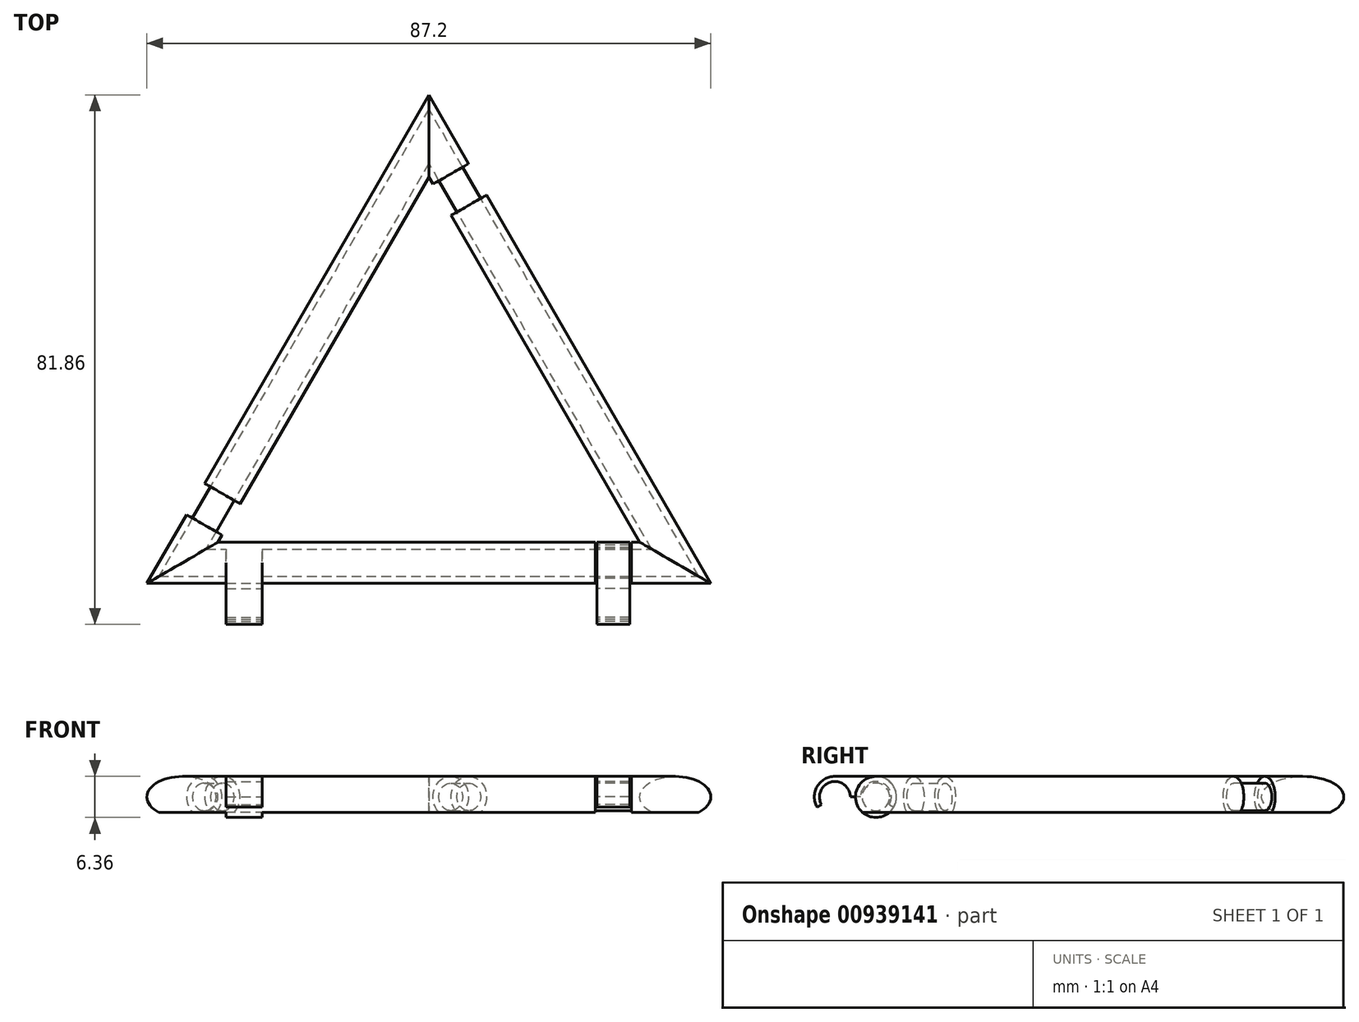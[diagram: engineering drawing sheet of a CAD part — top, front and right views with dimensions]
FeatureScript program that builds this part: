
annotation { "Feature Type Name" : "Feature", "Feature Type Description" : "" }
export const myFeature = defineFeature(function(context is Context, id is Id, definition is map)
    precondition{}
    {
        {
            var Q0;
            Q0=qCreatedBy(makeId("Top.planeOp"),FACE);
            var sketch = newSketch(context, id + "F0", { "sketchPlane" : qUnion([Q0])});
            skCircle(sketch, "E0.cCircle", {"center": v(0, 0) * mm, "radius": 44 * mm, "construction": true});
            skLineSegment(sketch, "E0.0", {"start": v(0, 44) * mm, "end": v(38.1, -22) * mm});
            skLineSegment(sketch, "E0.1", {"start": v(38.1, -22) * mm, "end": v(-38.1, -22) * mm});
            skLineSegment(sketch, "E0.2", {"start": v(-38.1, -22) * mm, "end": v(0, 44) * mm});
            skPoint(sketch, "E1", {"position": v(31.33, -22) * mm});
            skPoint(sketch, "E2", {"position": v(34.72, -16.13) * mm});
            skPoint(sketch, "E3", {"position": v(-31.33, -22) * mm});
            skPoint(sketch, "E4", {"position": v(-34.72, -16.13) * mm});
            skPoint(sketch, "E5", {"position": v(-3.38, 38.13) * mm});
            skPoint(sketch, "E6", {"position": v(3.38, 38.13) * mm});
            skPoint(sketch, "E7", {"position": v(6.05, 33.51) * mm});
            skPoint(sketch, "E8", {"position": v(-6.18, 33.3) * mm});
            skPoint(sketch, "E9", {"position": v(31.92, -11.3) * mm});
            skPoint(sketch, "E10", {"position": v(25.74, -22) * mm});
            skPoint(sketch, "E11", {"position": v(-25.74, -22) * mm});
            skPoint(sketch, "E12", {"position": v(-32.05, -11.52) * mm});
            skPoint(sketch, "E13", {"position": v(-31.08, -22) * mm});
            skPoint(sketch, "E14", {"position": v(-26, -22) * mm});
            skPoint(sketch, "E15", {"position": v(-34.59, -15.91) * mm});
            skPoint(sketch, "E16", {"position": v(-31.92, -11.3) * mm});
            skPoint(sketch, "E17", {"position": v(31.08, -22) * mm});
            skPoint(sketch, "E18", {"position": v(26, -22) * mm});
            skPoint(sketch, "E19", {"position": v(32.05, -11.52) * mm});
            skPoint(sketch, "E20", {"position": v(34.59, -15.91) * mm});
            skCircle(sketch, "E21", {"center": v(0, -22) * mm, "radius": 3.18 * mm});
            skLineSegment(sketch, "E22", {"start": v(0, -22) * mm, "end": v(0, -25.17) * mm});
            skCircle(sketch, "E23", {"center": v(38.1, -22) * mm, "radius": 3.18 * mm});
            skCircle(sketch, "E24", {"center": v(-38.1, -22) * mm, "radius": 3.18 * mm});
            skCircle(sketch, "E25", {"center": v(0, 44) * mm, "radius": 3.18 * mm});
            skPoint(sketch, "E26", {"position": v(3.51, 37.91) * mm});
            skPoint(sketch, "E27", {"position": v(6.18, 33.3) * mm});
            skPoint(sketch, "E28", {"position": v(-3.51, 37.91) * mm});
            skPoint(sketch, "E29", {"position": v(-6.05, 33.51) * mm});
            skLineSegment(sketch, "E30", {"start": v(-38.1, -18.82) * mm, "end": v(38.1, -18.82) * mm});
            skLineSegment(sketch, "E31", {"start": v(35.35, -23.58) * mm, "end": v(-2.75, 42.4) * mm});
            skLineSegment(sketch, "E32", {"start": v(-35.35, -23.58) * mm, "end": v(2.75, 42.4) * mm});
            skLineSegment(sketch, "E33", {"start": v(-35.35, -17.23) * mm, "end": v(-32.6, -18.82) * mm});
            skLineSegment(sketch, "E34", {"start": v(-32.6, -18.82) * mm, "end": v(-32.6, -22) * mm});
            skLineSegment(sketch, "E35", {"start": v(32.6, -18.82) * mm, "end": v(32.6, -22) * mm});
            skLineSegment(sketch, "E36", {"start": v(32.6, -18.82) * mm, "end": v(35.35, -17.23) * mm});
            skLineSegment(sketch, "E37", {"start": v(0, 37.64) * mm, "end": v(2.75, 39.23) * mm});
            skLineSegment(sketch, "E38", {"start": v(0, 37.64) * mm, "end": v(-2.75, 39.23) * mm});
            skSolve(sketch);
        }
        {
            var Q0;
            Q0=qCreatedBy(makeId("Right.planeOp"),FACE);
            var sketch = newSketch(context, id + "F1", { "sketchPlane" : qUnion([Q0])});
            skCircle(sketch, "E39", {"center": v(-22, 0) * mm, "radius": 3.18 * mm});
            skLineSegment(sketch, "E40", {"start": v(-22, 0) * mm, "end": v(-22, -3.18) * mm});
            skCircle(sketch, "E41.cCircle", {"center": v(-22, -1.59) * mm, "radius": 1.59 * mm, "construction": true});
            skLineSegment(sketch, "E41.0", {"start": v(-22, 0) * mm, "end": v(-20.62, -2.38) * mm});
            skLineSegment(sketch, "E41.1", {"start": v(-20.62, -2.38) * mm, "end": v(-23.37, -2.38) * mm});
            skLineSegment(sketch, "E41.2", {"start": v(-23.37, -2.38) * mm, "end": v(-22, 0) * mm});
            skLineSegment(sketch, "E42", {"start": v(-23.37, -2.38) * mm, "end": v(-24.1, -2.38) * mm});
            skLineSegment(sketch, "E43", {"start": v(-20.62, -2.38) * mm, "end": v(-19.9, -2.38) * mm});
            skSolve(sketch);
        }
        {
            var Q0;
            Q0=makeQuery(id+"F1.imprint","IMPRINT",FACE,{"disambiguationData":[TD([[makeQuery(id+"F1.imprint","IMPRINT",EDGE,{"derivedFrom":sQuery(id+"F1.wireOp",EDGE,"E41.0")}),1.0]])]});
            var Q1;
            {var subQ0=sQuery(id+"F1.wireOp",EDGE,"E41.2");Q1=makeQuery(id+"F1.imprint","IMPRINT",FACE,{"disambiguationData":[TD([[makeQuery(id+"F1.imprint","IMPRINT",EDGE,{"derivedFrom":subQ0}),-1.0]])]});}
            var Q2;
            {var subQ0=sQuery(id+"F1.wireOp",EDGE,"E41.0");Q2=makeQuery(id+"F1.imprint","IMPRINT",FACE,{"disambiguationData":[TD([[makeQuery(id+"F1.imprint","IMPRINT",EDGE,{"derivedFrom":subQ0}),-1.0]])]});}
            var Q3;
            Q3=sQuery(id+"F0.wireOp",EDGE,"E0.0");
            var Q4;
            Q4=sQuery(id+"F0.wireOp",EDGE,"E0.1");
            var Q5;
            Q5=sQuery(id+"F0.wireOp",EDGE,"E0.2");
            sweep(context, id + "F2", {"profiles" : qUnion([Q0, Q1, Q2]), "path" : qUnion([Q3, Q4, Q5])});
        }
        {
            var Q0;
            Q0=qCreatedBy(makeId("Right.planeOp"),FACE);
            var sketch = newSketch(context, id + "F3", { "sketchPlane" : qUnion([Q0])});
            skArc(sketch, "E44", {"start": v(-25.17, 0) * mm, "mid": v(-19.75, -2.25) * mm, "end": v(-22, 3.18) * mm});
            skCircle(sketch, "E45", {"center": v(-22, 0) * mm, "radius": 2.38 * mm});
            skArc(sketch, "E46", {"start": v(-28.35, 3.18) * mm, "mid": v(-30.6, -2.25) * mm, "end": v(-25.17, 0) * mm});
            skCircle(sketch, "E47", {"center": v(-28.35, 0) * mm, "radius": 2.38 * mm});
            skLineSegment(sketch, "E48", {"start": v(-22, 3.18) * mm, "end": v(-28.35, 3.18) * mm});
            skLineSegment(sketch, "E49", {"start": v(-24.38, 0) * mm, "end": v(-25.97, 0) * mm});
            skLineSegment(sketch, "E50", {"start": v(-28.35, 0) * mm, "end": v(-31.1, -1.59) * mm});
            skLineSegment(sketch, "E51", {"start": v(-22, 0) * mm, "end": v(-19.25, -1.59) * mm});
            skCircle(sketch, "E52.0", {"center": v(-22, 0) * mm, "radius": 2.13 * mm});
            skSolve(sketch);
        }
        {
            var Q0;
            Q0=qCreatedBy(makeId("Front.planeOp"),FACE);
            var sketch = newSketch(context, id + "F4", { "sketchPlane" : qUnion([Q0])});
            skLineSegment(sketch, "E53", {"start": v(0, 0) * mm, "end": v(0, 31.72) * mm});
            skSolve(sketch);
        }
        {
            var Q0;
            {var subQ0=sQuery(id+"F3.wireOp",EDGE,"E48");Q0=makeQuery(id+"F3.imprint","IMPRINT",FACE,{"disambiguationData":[TD([[makeQuery(id+"F3.imprint","IMPRINT",EDGE,{"derivedFrom":subQ0}),1.0]])]});}
            var Q1;
            {var subQ0=sQuery(id+"F3.wireOp",EDGE,"E49");var subQ5=sQuery(id+"F3.wireOp",EDGE,"E45");var subQ6=makeQuery(id+"F3.imprint","INTERSECT",VERTEX,{"derivedFrom":[subQ5,subQ0]});Q1=makeQuery(id+"F3.imprint","IMPRINT",FACE,{"disambiguationData":[TD([[makeQuery(id+"F3.imprint","IMPRINT",EDGE,{"disambiguationData":[TD([[subQ6,-1.0]])],"derivedFrom":subQ5}),-1.0]])]});}
            var Q2;
            Q2=makeQuery(id+"F3.imprint","IMPRINT",FACE,{"disambiguationData":[TD([[makeQuery(id+"F3.imprint","IMPRINT",EDGE,{"derivedFrom":sQuery(id+"F3.wireOp",EDGE,"E52.0")}),-1.0]])]});
            var Q3;
            Q3=sQuery(id+"F0.wireOp",VERTEX,"E1");
            var Q4;
            Q4=sQuery(id+"F0.wireOp",VERTEX,"E10");
            extrude(context, id + "F5", {"entities" : qUnion([Q0, Q1, Q2]), "endBound" : BoundingType.UP_TO_VERTEX, "depth" : 31.5 * mm, "endBoundEntityVertex" : qUnion([Q3]), "offsetDistance" : 25.4 * mm, "hasSecondDirection" : true, "secondDirectionBound" : SecondDirectionBoundingType.UP_TO_VERTEX, "secondDirectionOppositeDirection" : false, "secondDirectionDepth" : 26.92 * mm, "secondDirectionBoundEntityVertex" : qUnion([Q4])});
        }
        {
            var Q0;
            {var subQ0=sQuery(id+"F3.wireOp",EDGE,"E48");Q0=makeQuery(id+"F3.imprint","IMPRINT",FACE,{"disambiguationData":[TD([[makeQuery(id+"F3.imprint","IMPRINT",EDGE,{"derivedFrom":subQ0}),1.0]])]});}
            var Q1;
            {var subQ0=sQuery(id+"F3.wireOp",EDGE,"E49");var subQ5=sQuery(id+"F3.wireOp",EDGE,"E45");var subQ6=makeQuery(id+"F3.imprint","INTERSECT",VERTEX,{"derivedFrom":[subQ5,subQ0]});Q1=makeQuery(id+"F3.imprint","IMPRINT",FACE,{"disambiguationData":[TD([[makeQuery(id+"F3.imprint","IMPRINT",EDGE,{"disambiguationData":[TD([[subQ6,-1.0]])],"derivedFrom":subQ5}),-1.0]])]});}
            var Q2;
            Q2=makeQuery(id+"F3.imprint","IMPRINT",FACE,{"disambiguationData":[TD([[makeQuery(id+"F3.imprint","IMPRINT",EDGE,{"derivedFrom":sQuery(id+"F3.wireOp",EDGE,"E52.0")}),-1.0]])]});
            var Q3;
            Q3=sQuery(id+"F0.wireOp",VERTEX,"E3");
            var Q4;
            Q4=sQuery(id+"F0.wireOp",VERTEX,"E11");
            extrude(context, id + "F6", {"entities" : qUnion([Q0, Q1, Q2]), "operationType" : NewBodyOperationType.ADD, "endBound" : BoundingType.UP_TO_VERTEX, "oppositeDirection" : true, "depth" : 25.4 * mm, "endBoundEntityVertex" : qUnion([Q3]), "offsetDistance" : 25.4 * mm, "hasSecondDirection" : true, "secondDirectionBound" : SecondDirectionBoundingType.UP_TO_VERTEX, "secondDirectionOppositeDirection" : true, "secondDirectionDepth" : 25.4 * mm, "secondDirectionBoundEntityVertex" : qUnion([Q4])});
        }
        {
            var Q0;
            Q0=makeQuery(id+"F5.opExtrude","SWEPT_BODY",BODY,{"disambiguationData":[OSD([sQuery(id+"F3.wireOp",EDGE,"E44"),sQuery(id+"F3.wireOp",EDGE,"E46"),sQuery(id+"F3.wireOp",EDGE,"E47"),sQuery(id+"F3.wireOp",EDGE,"E48"),sQuery(id+"F3.wireOp",EDGE,"E49"),sQuery(id+"F3.wireOp",EDGE,"E50"),sQuery(id+"F3.wireOp",EDGE,"E52.0")])]});
            var Q1;
            Q1=makeQuery(id+"F6.opExtrude","SWEPT_BODY",BODY,{"disambiguationData":[OSD([sQuery(id+"F3.wireOp",EDGE,"E44"),sQuery(id+"F3.wireOp",EDGE,"E46"),sQuery(id+"F3.wireOp",EDGE,"E47"),sQuery(id+"F3.wireOp",EDGE,"E48"),sQuery(id+"F3.wireOp",EDGE,"E49"),sQuery(id+"F3.wireOp",EDGE,"E50"),sQuery(id+"F3.wireOp",EDGE,"E52.0")])]});
            var Q2;
            Q2=sQuery(id+"F4.wireOp",EDGE,"E53");
            circularPattern(context, id + "F7", {"entities" : qUnion([Q0, Q1]), "axis" : qUnion([Q2]), "angle" : 360 * degree, "instanceCount" : 3, "equalSpace" : true});
        }
        {
            var Q0;
            Q0=makeQuery(id+"F7.opPattern","COPY",BODY,{"derivedFrom":makeQuery(id+"F5.opExtrude","SWEPT_BODY",BODY,{"disambiguationData":[OSD([sQuery(id+"F3.wireOp",EDGE,"E44"),sQuery(id+"F3.wireOp",EDGE,"E46"),sQuery(id+"F3.wireOp",EDGE,"E47"),sQuery(id+"F3.wireOp",EDGE,"E48"),sQuery(id+"F3.wireOp",EDGE,"E49"),sQuery(id+"F3.wireOp",EDGE,"E50"),sQuery(id+"F3.wireOp",EDGE,"E52.0")])]}),"instanceName":"2"});
            var Q1;
            Q1=makeQuery(id+"F7.opPattern","COPY",BODY,{"derivedFrom":makeQuery(id+"F6.opExtrude","SWEPT_BODY",BODY,{"disambiguationData":[OSD([sQuery(id+"F3.wireOp",EDGE,"E44"),sQuery(id+"F3.wireOp",EDGE,"E46"),sQuery(id+"F3.wireOp",EDGE,"E47"),sQuery(id+"F3.wireOp",EDGE,"E48"),sQuery(id+"F3.wireOp",EDGE,"E49"),sQuery(id+"F3.wireOp",EDGE,"E50"),sQuery(id+"F3.wireOp",EDGE,"E52.0")])]}),"instanceName":"2"});
            var Q2;
            Q2=makeQuery(id+"F7.opPattern","COPY",BODY,{"derivedFrom":makeQuery(id+"F5.opExtrude","SWEPT_BODY",BODY,{"disambiguationData":[OSD([sQuery(id+"F3.wireOp",EDGE,"E44"),sQuery(id+"F3.wireOp",EDGE,"E46"),sQuery(id+"F3.wireOp",EDGE,"E47"),sQuery(id+"F3.wireOp",EDGE,"E48"),sQuery(id+"F3.wireOp",EDGE,"E49"),sQuery(id+"F3.wireOp",EDGE,"E50"),sQuery(id+"F3.wireOp",EDGE,"E52.0")])]}),"instanceName":"1"});
            var Q3;
            Q3=makeQuery(id+"F7.opPattern","COPY",BODY,{"derivedFrom":makeQuery(id+"F6.opExtrude","SWEPT_BODY",BODY,{"disambiguationData":[OSD([sQuery(id+"F3.wireOp",EDGE,"E44"),sQuery(id+"F3.wireOp",EDGE,"E46"),sQuery(id+"F3.wireOp",EDGE,"E47"),sQuery(id+"F3.wireOp",EDGE,"E48"),sQuery(id+"F3.wireOp",EDGE,"E49"),sQuery(id+"F3.wireOp",EDGE,"E50"),sQuery(id+"F3.wireOp",EDGE,"E52.0")])]}),"instanceName":"1"});
            var Q4;
            Q4=makeQuery(id+"F5.opExtrude","SWEPT_BODY",BODY,{"disambiguationData":[OSD([sQuery(id+"F3.wireOp",EDGE,"E44"),sQuery(id+"F3.wireOp",EDGE,"E46"),sQuery(id+"F3.wireOp",EDGE,"E47"),sQuery(id+"F3.wireOp",EDGE,"E48"),sQuery(id+"F3.wireOp",EDGE,"E49"),sQuery(id+"F3.wireOp",EDGE,"E50"),sQuery(id+"F3.wireOp",EDGE,"E52.0")])]});
            var Q5;
            Q5=makeQuery(id+"F6.opExtrude","SWEPT_BODY",BODY,{"disambiguationData":[OSD([sQuery(id+"F3.wireOp",EDGE,"E44"),sQuery(id+"F3.wireOp",EDGE,"E46"),sQuery(id+"F3.wireOp",EDGE,"E47"),sQuery(id+"F3.wireOp",EDGE,"E48"),sQuery(id+"F3.wireOp",EDGE,"E49"),sQuery(id+"F3.wireOp",EDGE,"E50"),sQuery(id+"F3.wireOp",EDGE,"E52.0")])]});
            var Q6;
            Q6=makeQuery(id+"F2.opSweep","SWEPT_BODY",BODY,{"disambiguationData":[OSD([sQuery(id+"F0.wireOp",EDGE,"E0.2"),sQuery(id+"F1.wireOp",EDGE,"E39"),sQuery(id+"F1.wireOp",EDGE,"E41.1"),sQuery(id+"F1.wireOp",EDGE,"E42"),sQuery(id+"F1.wireOp",EDGE,"E43")])]});
            booleanBodies(context, id + "F8", {"operationType" : BooleanOperationType.SUBTRACTION, "tools" : qUnion([Q0, Q1, Q2, Q3, Q4, Q5]), "targets" : qUnion([Q6])});
        }
        {
            var Q0;
            {var subQ0=sQuery(id+"F3.wireOp",EDGE,"E48");Q0=makeQuery(id+"F3.imprint","IMPRINT",FACE,{"disambiguationData":[TD([[makeQuery(id+"F3.imprint","IMPRINT",EDGE,{"derivedFrom":subQ0}),1.0]])]});}
            var Q1;
            Q1=sQuery(id+"F0.wireOp",VERTEX,"E17");
            var Q2;
            Q2=sQuery(id+"F0.wireOp",VERTEX,"E18");
            extrude(context, id + "F9", {"entities" : qUnion([Q0]), "endBound" : BoundingType.UP_TO_VERTEX, "depth" : 25.4 * mm, "endBoundEntityVertex" : qUnion([Q1]), "offsetDistance" : 25.4 * mm, "hasSecondDirection" : true, "secondDirectionBound" : SecondDirectionBoundingType.UP_TO_VERTEX, "secondDirectionOppositeDirection" : false, "secondDirectionDepth" : 25.4 * mm, "secondDirectionBoundEntityVertex" : qUnion([Q2])});
        }
    });
